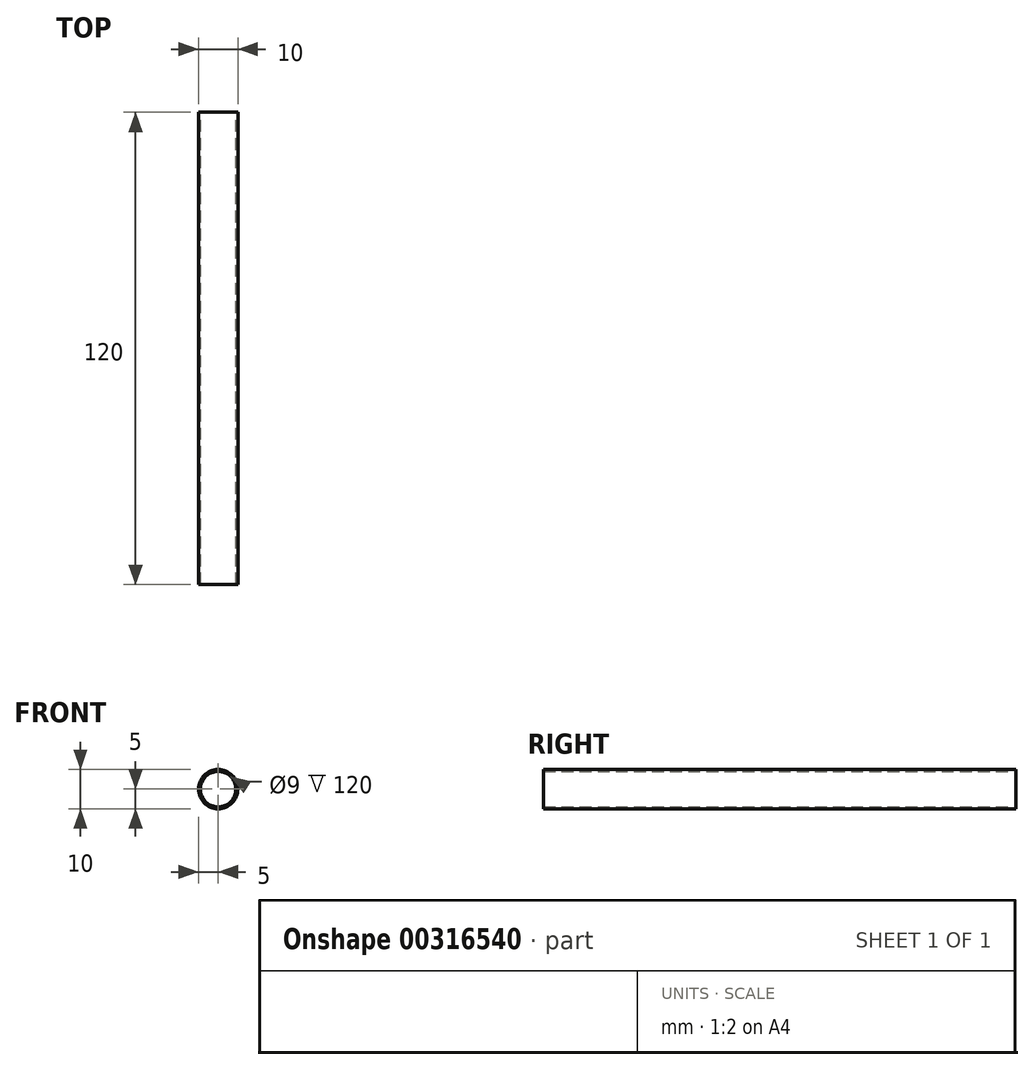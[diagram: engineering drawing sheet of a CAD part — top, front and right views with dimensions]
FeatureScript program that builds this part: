
annotation { "Feature Type Name" : "Feature", "Feature Type Description" : "" }
export const myFeature = defineFeature(function(context is Context, id is Id, definition is map)
    precondition{}
    {
        {
            var Q0;
            Q0=qCreatedBy(makeId("Front.planeOp"),FACE);
            var sketch = newSketch(context, id + "F0", { "sketchPlane" : qUnion([Q0])});
            skCircle(sketch, "E0", {"center": v(0, 0) * mm, "radius": 5 * mm});
            skCircle(sketch, "E1", {"center": v(0, 0) * mm, "radius": 4.5 * mm});
            skSolve(sketch);
        }
        {
            var Q0;
            Q0=makeQuery(id+"F0.imprint","IMPRINT",FACE,{"disambiguationData":[TD([[makeQuery(id+"F0.imprint","IMPRINT",EDGE,{"derivedFrom":sQuery(id+"F0.wireOp",EDGE,"E0")}),1.0]])]});
            extrude(context, id + "F1", {"entities" : qUnion([Q0]), "flatOperationType" : FlatOperationType.REMOVE, "offsetDistance" : 25 * mm, "depth" : 120 * mm, "domain" : OperationDomain.MODEL});
        }
    });
